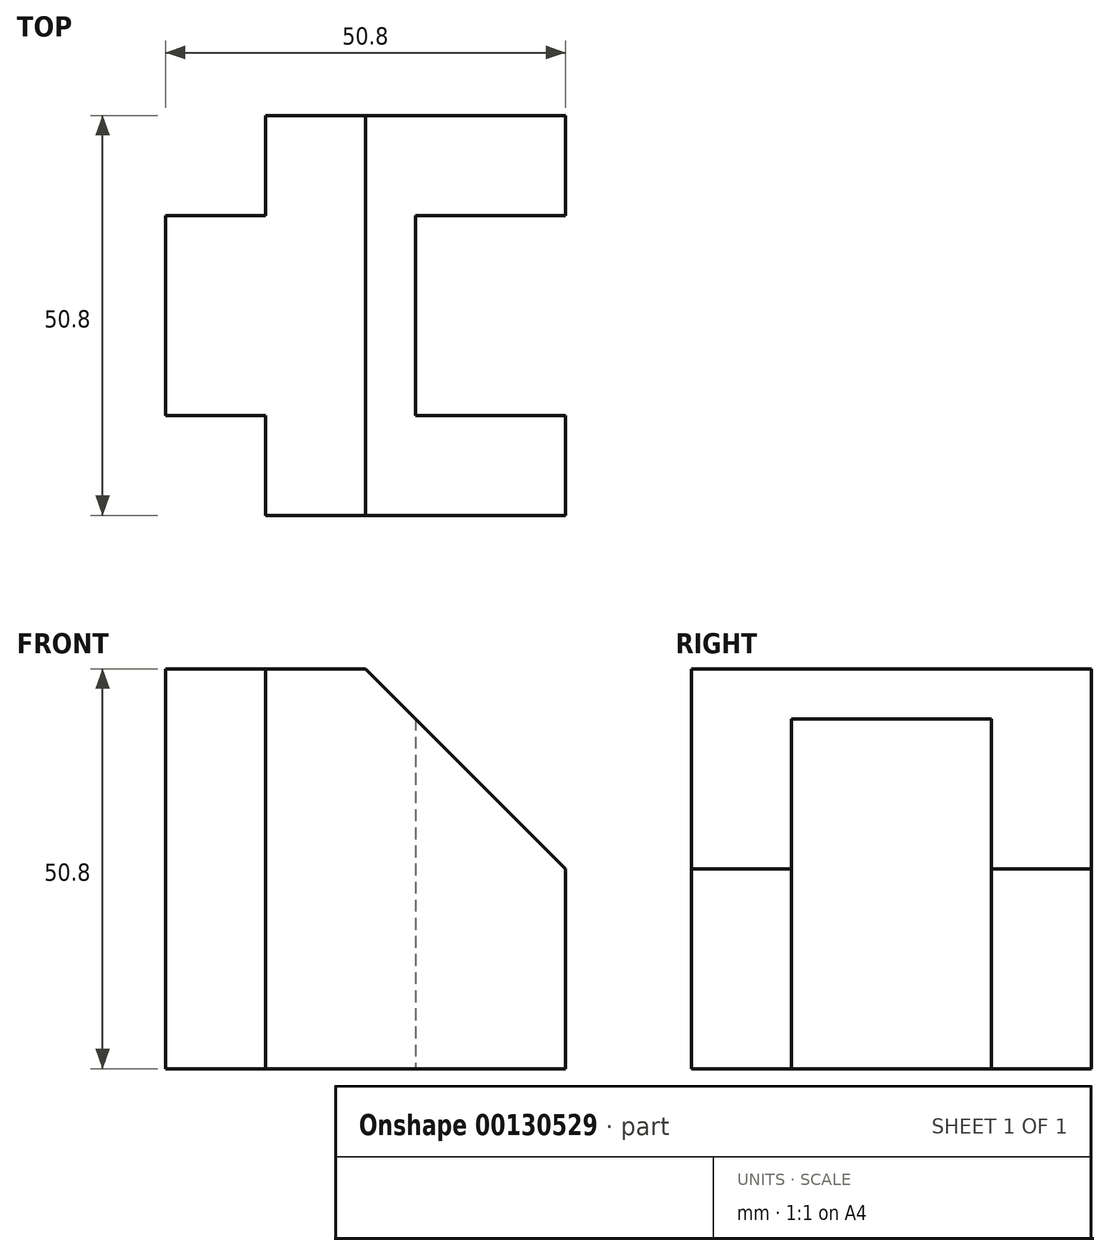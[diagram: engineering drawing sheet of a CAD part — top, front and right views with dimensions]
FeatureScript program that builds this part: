
annotation { "Feature Type Name" : "Feature", "Feature Type Description" : "" }
export const myFeature = defineFeature(function(context is Context, id is Id, definition is map)
    precondition{}
    {
        {
            var Q0;
            Q0=qCreatedBy(makeId("Top.planeOp"),FACE);
            var sketch = newSketch(context, id + "F0", { "sketchPlane" : qUnion([Q0])});
            skLineSegment(sketch, "E0", {"start": v(0, -12.7) * mm, "end": v(0, 12.7) * mm});
            skLineSegment(sketch, "E1", {"start": v(0, 12.7) * mm, "end": v(19.05, 12.7) * mm});
            skLineSegment(sketch, "E2", {"start": v(19.05, 12.7) * mm, "end": v(19.05, 25.4) * mm});
            skLineSegment(sketch, "E3", {"start": v(19.05, 25.4) * mm, "end": v(-19.05, 25.4) * mm});
            skLineSegment(sketch, "E4", {"start": v(-19.05, 25.4) * mm, "end": v(-19.05, 12.7) * mm});
            skLineSegment(sketch, "E5", {"start": v(-19.05, 12.7) * mm, "end": v(-31.75, 12.7) * mm});
            skLineSegment(sketch, "E6", {"start": v(-31.75, 12.7) * mm, "end": v(-31.75, -12.7) * mm});
            skLineSegment(sketch, "E7", {"start": v(-31.75, -12.7) * mm, "end": v(-19.05, -12.7) * mm});
            skLineSegment(sketch, "E8", {"start": v(-19.05, -12.7) * mm, "end": v(-19.05, -25.4) * mm});
            skLineSegment(sketch, "E9", {"start": v(-19.05, -25.4) * mm, "end": v(19.05, -25.4) * mm});
            skLineSegment(sketch, "E10", {"start": v(19.05, -25.4) * mm, "end": v(19.05, -12.7) * mm});
            skLineSegment(sketch, "E11", {"start": v(19.05, -12.7) * mm, "end": v(0, -12.7) * mm});
            skSolve(sketch);
        }
        {
            var Q0;
            Q0=makeQuery(id+"F0.imprint","IMPRINT",FACE,{"disambiguationData":[TD([[makeQuery(id+"F0.imprint","IMPRINT",EDGE,{"derivedFrom":sQuery(id+"F0.wireOp",EDGE,"E0")}),1.0]])]});
            extrude(context, id + "F1", {"entities" : qUnion([Q0]), "endBound" : BoundingType.SYMMETRIC, "depth" : 50.8 * mm});
        }
        {
            var Q0;
            Q0=makeQuery(id+"F1.opExtrude","SWEPT_FACE",FACE,{"disambiguationData":[OSD([sQuery(id+"F0.wireOp",EDGE,"E9")])]});
            var sketch = newSketch(context, id + "F2", { "sketchPlane" : qUnion([Q0])});
            skLineSegment(sketch, "E12.0", {"start": v(19.05, 25.4) * mm, "end": v(19.05, -25.4) * mm});
            skLineSegment(sketch, "E12.1", {"start": v(-19.05, 25.4) * mm, "end": v(19.05, 25.4) * mm});
            skPoint(sketch, "E13", {"position": v(19.05, 0) * mm});
            skLineSegment(sketch, "E14.0", {"start": v(-31.75, 25.4) * mm, "end": v(-19.05, 25.4) * mm});
            skPoint(sketch, "E15", {"position": v(-6.35, 25.4) * mm});
            skLineSegment(sketch, "E16", {"start": v(-6.35, 25.4) * mm, "end": v(19.05, 0) * mm});
            skSolve(sketch);
        }
        {
            var Q0;
            Q0 = qSketchRegion(id + "F2", true);
            extrude(context, id + "F3", {"entities" : qUnion([Q0]), "operationType" : NewBodyOperationType.REMOVE, "endBound" : BoundingType.THROUGH_ALL, "oppositeDirection" : true, "depth" : 25.4 * mm});
        }
    });
